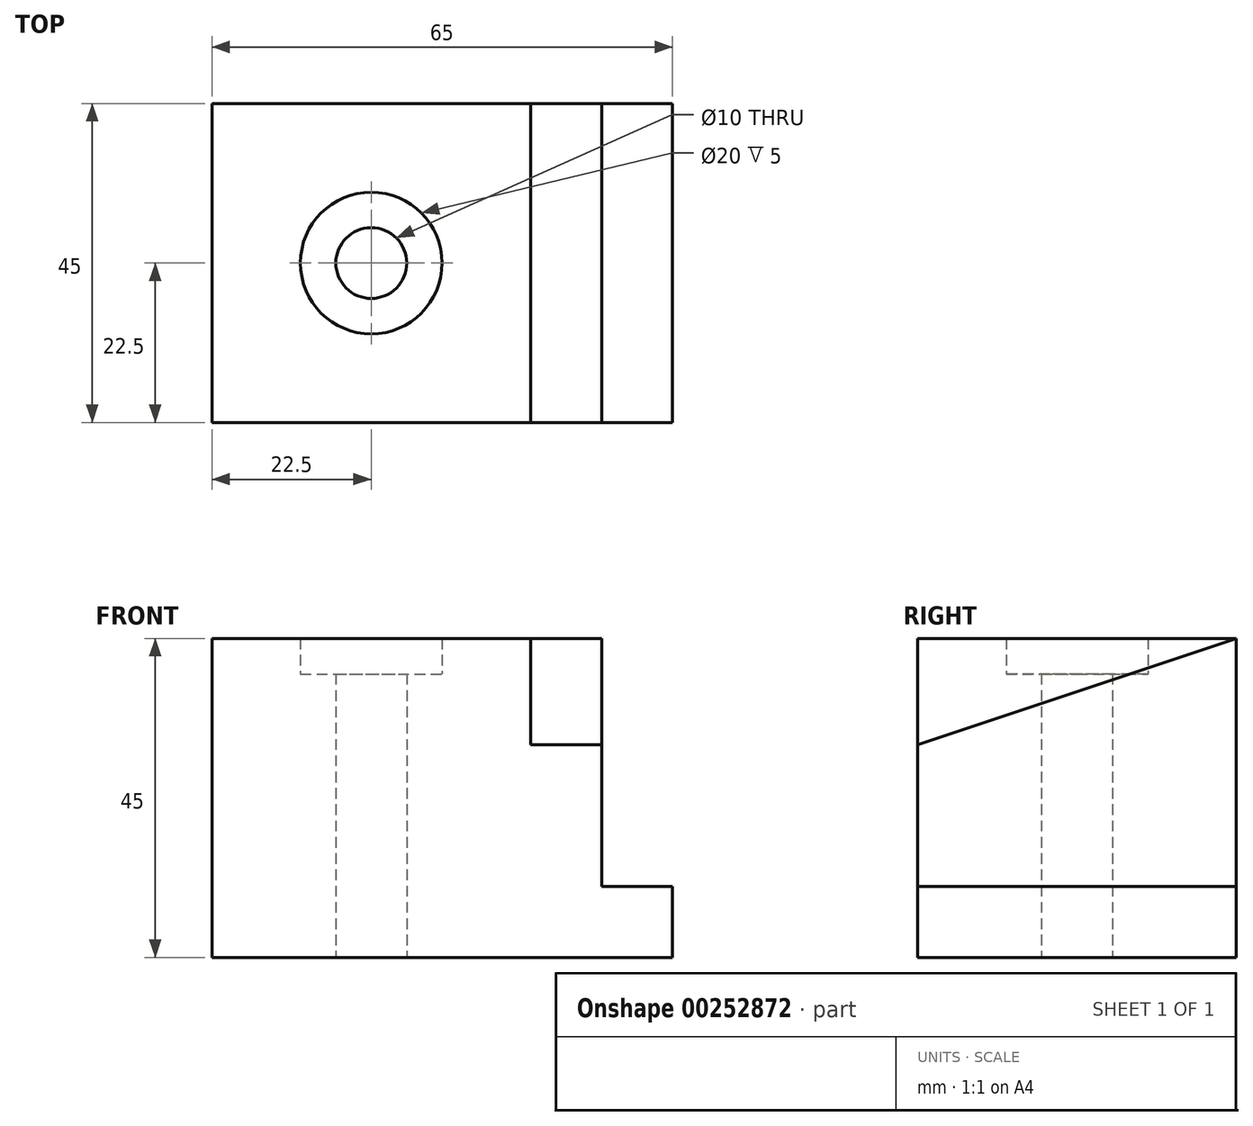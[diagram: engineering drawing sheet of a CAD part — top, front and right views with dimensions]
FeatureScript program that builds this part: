
annotation { "Feature Type Name" : "Feature", "Feature Type Description" : "" }
export const myFeature = defineFeature(function(context is Context, id is Id, definition is map)
    precondition{}
    {
        {
            var Q0;
            Q0=qCreatedBy(makeId("Front.planeOp"),FACE);
            var sketch = newSketch(context, id + "F0", { "sketchPlane" : qUnion([Q0])});
            skLineSegment(sketch, "E0", {"start": v(0, 0) * mm, "end": v(0, 45) * mm});
            skLineSegment(sketch, "E1", {"start": v(0, 45) * mm, "end": v(55, 45) * mm});
            skLineSegment(sketch, "E2", {"start": v(55, 45) * mm, "end": v(55, 10) * mm});
            skLineSegment(sketch, "E3", {"start": v(55, 10) * mm, "end": v(65, 10) * mm});
            skLineSegment(sketch, "E4", {"start": v(65, 10) * mm, "end": v(65, 0) * mm});
            skLineSegment(sketch, "E5", {"start": v(65, 0) * mm, "end": v(0, 0) * mm});
            skSolve(sketch);
        }
        {
            var Q0;
            Q0=makeQuery(id+"F0.imprint","IMPRINT",FACE,{"disambiguationData":[TD([[makeQuery(id+"F0.imprint","IMPRINT",EDGE,{"derivedFrom":sQuery(id+"F0.wireOp",EDGE,"E0")}),-1.0]])]});
            extrude(context, id + "F1", {"entities" : qUnion([Q0]), "depth" : 45 * mm});
        }
        {
            var Q0;
            Q0=makeQuery(id+"F1.opExtrude","SWEPT_FACE",FACE,{"disambiguationData":[OSD([sQuery(id+"F0.wireOp",EDGE,"E2")])]});
            var sketch = newSketch(context, id + "F2", { "sketchPlane" : qUnion([Q0])});
            skLineSegment(sketch, "E6", {"start": v(0, 45) * mm, "end": v(-45, 30) * mm});
            skSolve(sketch);
        }
        {
            var Q0;
            {var subQ0=sQuery(id+"F2.wireOp",EDGE,"E6");Q0=makeQuery(id+"F2.imprint","IMPRINT",FACE,{"disambiguationData":[TD([[makeQuery(id+"F2.imprint","IMPRINT",EDGE,{"derivedFrom":subQ0}),-1.0]])]});}
            extrude(context, id + "F3", {"entities" : qUnion([Q0]), "operationType" : NewBodyOperationType.REMOVE, "oppositeDirection" : true, "depth" : 10 * mm});
        }
        {
            var Q0;
            Q0=makeQuery(id+"F1.opExtrude","SWEPT_FACE",FACE,{"disambiguationData":[OSD([sQuery(id+"F0.wireOp",EDGE,"E1")])]});
            var sketch = newSketch(context, id + "F4", { "sketchPlane" : qUnion([Q0])});
            skPoint(sketch, "E7", {"position": v(22.5, -22.5) * mm});
            skSolve(sketch);
        }
        {
            var Q0;
            Q0=sQuery(id+"F4.wireOp",VERTEX,"E7");
            var Q1;
            Q1=makeQuery(id+"F1.opExtrude","SWEPT_BODY",BODY,{"disambiguationData":[OSD([sQuery(id+"F0.wireOp",EDGE,"E0"),sQuery(id+"F0.wireOp",EDGE,"E1"),sQuery(id+"F0.wireOp",EDGE,"E2"),sQuery(id+"F0.wireOp",EDGE,"E3"),sQuery(id+"F0.wireOp",EDGE,"E4"),sQuery(id+"F0.wireOp",EDGE,"E5")])]});
            hole(context, id + "F5", {"style" : HoleStyle.C_BORE, "endStyle" : HoleEndStyle.THROUGH, "holeDiameter" : 10 * mm, "cBoreDiameter" : 20 * mm, "cBoreDepth" : 5 * mm, "tappedDepth" : 12 * mm, "tapClearance" : 3, "locations" : qUnion([Q0]), "scope" : qUnion([Q1])});
        }
    });
